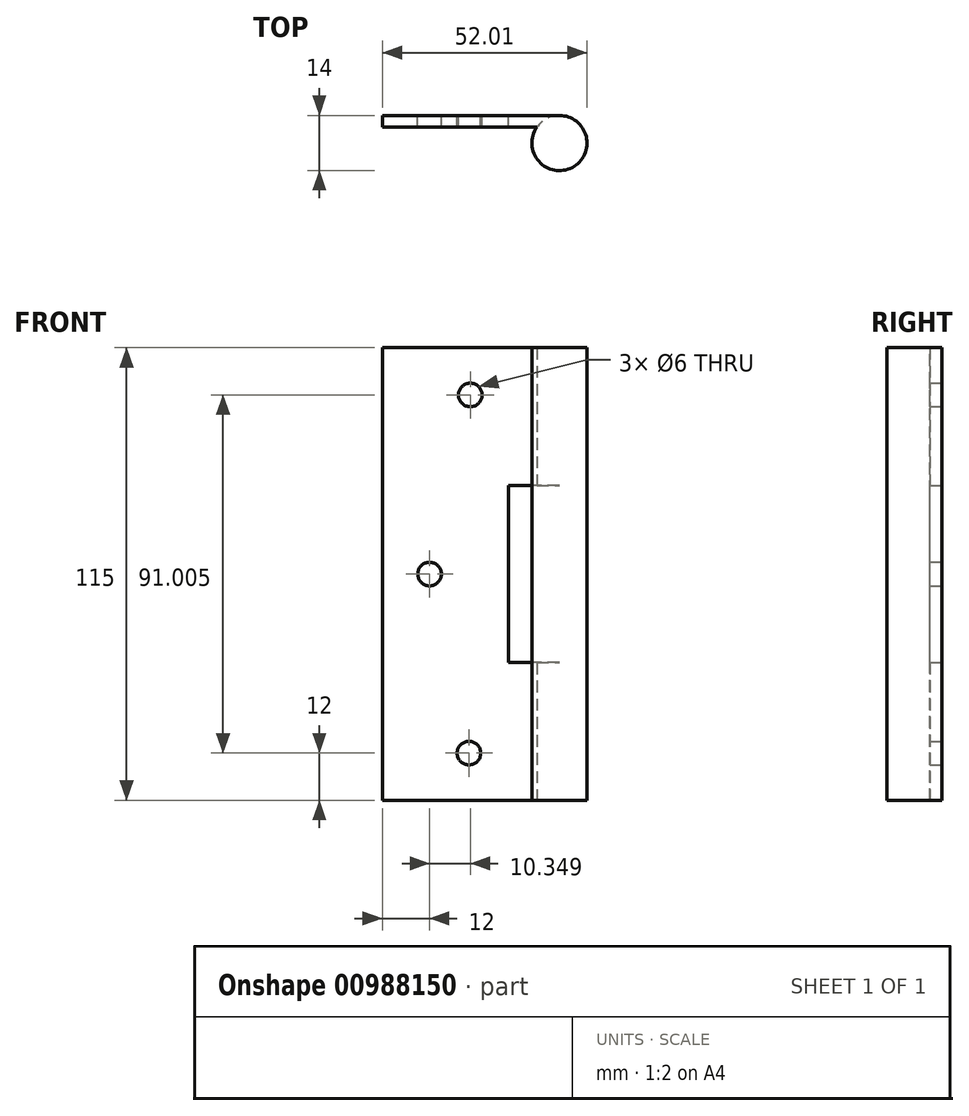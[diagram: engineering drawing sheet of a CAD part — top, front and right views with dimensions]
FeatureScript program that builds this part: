
annotation { "Feature Type Name" : "Feature", "Feature Type Description" : "" }
export const myFeature = defineFeature(function(context is Context, id is Id, definition is map)
    precondition{}
    {
        {
            var Q0;
            Q0=qCreatedBy(makeId("Front.planeOp"),FACE);
            var sketch = newSketch(context, id + "F0", { "sketchPlane" : qUnion([Q0])});
            skLineSegment(sketch, "E0", {"start": v(0, 0) * mm, "end": v(0, 115) * mm});
            skLineSegment(sketch, "E1", {"start": v(0, 115) * mm, "end": v(45, 115) * mm});
            skLineSegment(sketch, "E2", {"start": v(45, 115) * mm, "end": v(45, 80) * mm});
            skLineSegment(sketch, "E3", {"start": v(45, 0) * mm, "end": v(45, 35) * mm});
            skLineSegment(sketch, "E4", {"start": v(45, 35) * mm, "end": v(32, 35) * mm});
            skLineSegment(sketch, "E5", {"start": v(32, 35) * mm, "end": v(32, 80) * mm});
            skLineSegment(sketch, "E6", {"start": v(45, 80) * mm, "end": v(32, 80) * mm});
            skCircle(sketch, "E7", {"center": v(12, 57.5) * mm, "radius": 3 * mm});
            skCircle(sketch, "E8", {"center": v(22, 12) * mm, "radius": 3 * mm});
            skLineSegment(sketch, "E9", {"start": v(45, 0) * mm, "end": v(0, 0) * mm});
            skCircle(sketch, "E10", {"center": v(22.35, 103) * mm, "radius": 3 * mm});
            skPoint(sketch, "E11.orphan", {"position": v(22, 115) * mm});
            skSolve(sketch);
        }
        {
            var Q0;
            Q0=makeQuery(id+"F0.imprint","IMPRINT",FACE,{"disambiguationData":[TD([[makeQuery(id+"F0.imprint","IMPRINT",EDGE,{"derivedFrom":sQuery(id+"F0.wireOp",EDGE,"E0")}),-1.0]])]});
            extrude(context, id + "F1", {"entities" : qUnion([Q0]), "depth" : 3 * mm, "offsetDistance" : 25 * mm});
        }
        {
            var Q0;
            Q0=qCreatedBy(makeId("Top.planeOp"),FACE);
            var sketch = newSketch(context, id + "F2", { "sketchPlane" : qUnion([Q0])});
            skLineSegment(sketch, "E12", {"start": v(0, 0) * mm, "end": v(45, 0) * mm});
            skCircle(sketch, "E13", {"center": v(45, -7) * mm, "radius": 7 * mm});
            skSolve(sketch);
        }
        {
            var Q0;
            Q0=makeQuery(id+"F2.imprint","IMPRINT",FACE,{"disambiguationData":[TD([[makeQuery(id+"F2.imprint","IMPRINT",EDGE,{"derivedFrom":sQuery(id+"F2.wireOp",EDGE,"E13")}),1.0]])]});
            extrude(context, id + "F3", {"entities" : qUnion([Q0]), "operationType" : NewBodyOperationType.ADD, "depth" : 115 * mm, "offsetDistance" : 25 * mm});
        }
    });
